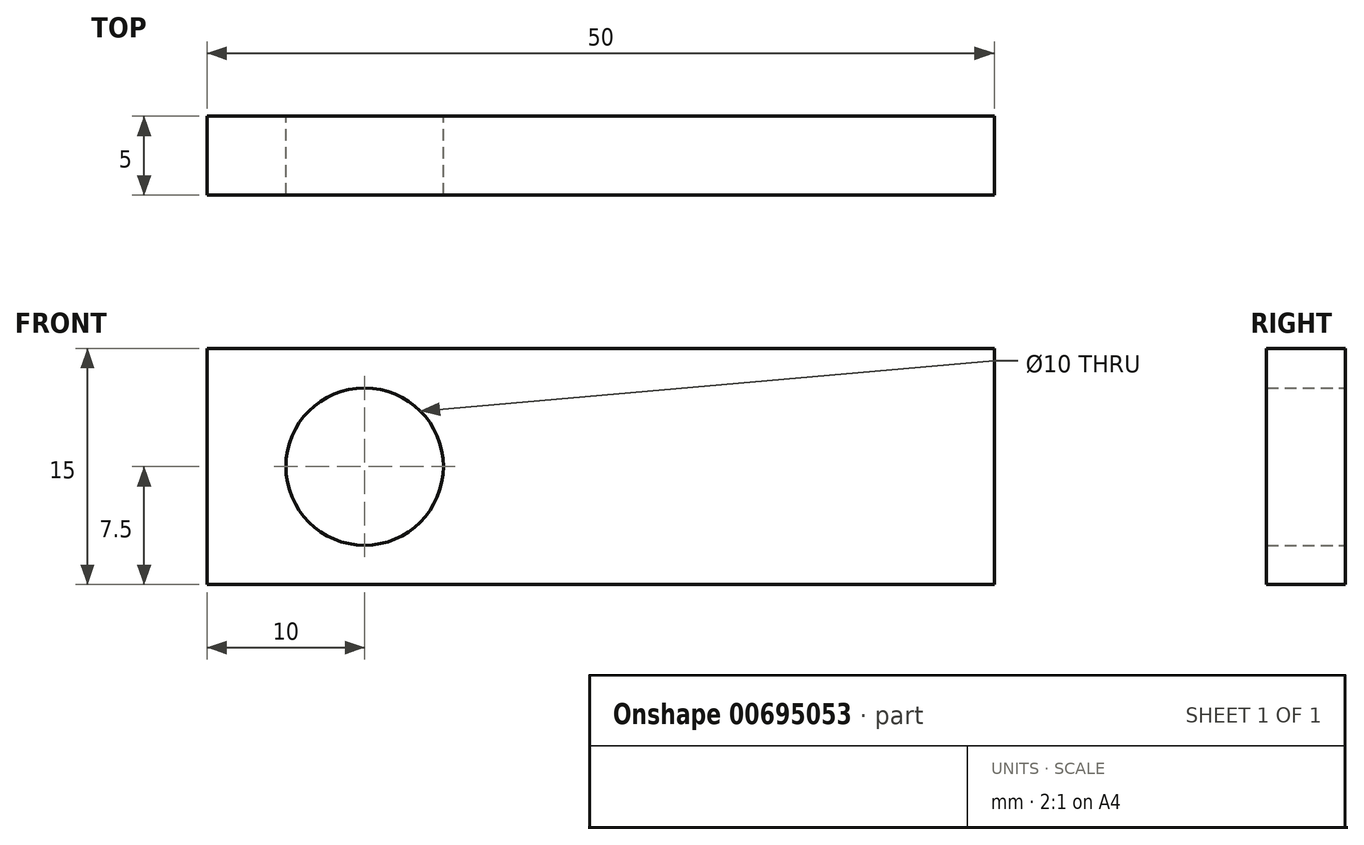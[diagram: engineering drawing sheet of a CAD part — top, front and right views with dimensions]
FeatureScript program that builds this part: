
annotation { "Feature Type Name" : "Feature", "Feature Type Description" : "" }
export const myFeature = defineFeature(function(context is Context, id is Id, definition is map)
    precondition{}
    {
        {
            var Q0;
            Q0=qCreatedBy(makeId("Front.planeOp"),FACE);
            var sketch = newSketch(context, id + "F0", { "sketchPlane" : qUnion([Q0])});
            skLineSegment(sketch, "E0.bottom", {"start": v(0, 0) * mm, "end": v(50, 0) * mm});
            skLineSegment(sketch, "E0.top", {"start": v(0, 15) * mm, "end": v(50, 15) * mm});
            skLineSegment(sketch, "E0.left", {"start": v(0, 0) * mm, "end": v(0, 15) * mm});
            skLineSegment(sketch, "E0.right", {"start": v(50, 0) * mm, "end": v(50, 15) * mm});
            skLineSegment(sketch, "E1", {"start": v(0, 7.5) * mm, "end": v(56.17, 7.5) * mm, "construction": true});
            skCircle(sketch, "E2", {"center": v(10, 7.5) * mm, "radius": 5 * mm});
            skPoint(sketch, "E3", {"position": v(50, 7.5) * mm});
            skSolve(sketch);
        }
        {
            var Q0;
            Q0 = qSketchRegion(id + "F0", true);
            extrude(context, id + "F1", {"entities" : qUnion([Q0]), "depth" : 5 * mm, "offsetDistance" : 25 * mm});
        }
    });
